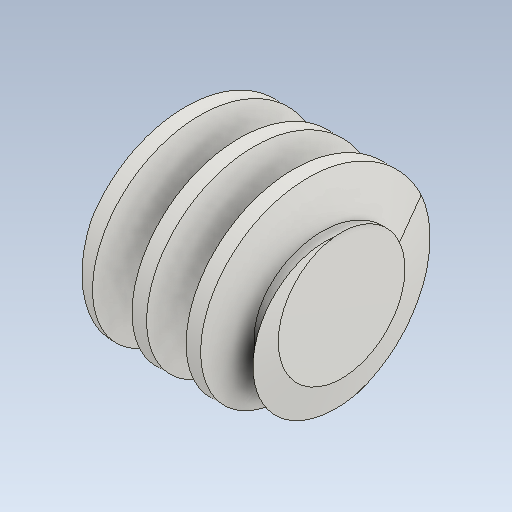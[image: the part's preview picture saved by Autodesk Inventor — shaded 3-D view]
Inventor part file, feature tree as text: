
AUTODESK INVENTOR PART (.ipt)
format: ipt  version: 2021 (Build 250183000, 183)  size: 291,840 bytes
history: native  units: mm (DEFAULTED — no unit token found)
features: other x6, chamfer x2, pattern_circular x2, extrude x1, sketch x1
ambient origin geometry x6: Origin, XZ Plane, X Axis, Y Axis, Z Axis, Center Point
bodies: Solid1 (feature_tree)
feature tree (12):
  extrude  "Base Body"  Depth=10.0mm
  chamfer  "Chamfer1"  Distance=40.0mm
  chamfer  "Chamfer2"  [1 undecoded]
  other  "Tooth Sketch"
  other  "Tooth"
  pattern_circular  "Tooth Pattern"  [2 undecoded]
  other  "Left Tooth"
  pattern_circular  "Left Tooth Pattern"  [2 undecoded]
  other  "Base Body Sketch"
  sketch  "Sketch5"  dims[d4=40.0mm d5=48.0mm d6=40.0mm d7=0.0mm d8=3.348526mm d9=9.2mm d10=3.348526mm d11=9.2mm d12=19.198622mm d14=3.1425mm d24=19.198622mm d25=31.574194mm d26=3.157419mm d27=14.8mm d28=20.0mm d29=24.24mm d30=12.629678mm d31=10.0mm d32=60.0mm d33=0.0mm d34=90.0deg d35=90.0deg d36=0.0mm d37=0.0mm d44=10.0mm d46=360.0deg d47=45.0deg d48=45.0deg d49=40.117556mm d50=0.0mm d54=0.0mm d56=0.0mm d59=40.0mm d60=10.0mm d61=0.0mm d62=12.629678mm d63=10.0mm d64=60.0mm d65=0.0mm d66=90.0deg d67=90.0deg d68=0.0mm d69=0.0mm d70=10.0mm d71=10.0mm d72=10.0mm d73=360.0deg d75=10.0mm d76=10.0mm d77=0.0mm d79=40.117556mm d80=0.0mm]
  other  "Srf1"
  other  "Pitch Diameter"
note: 5 required parameter values undecoded (feature->parameter linkage not recoverable at this tier; creation-order binding heuristic only, values carry confidence <= 0.55)
